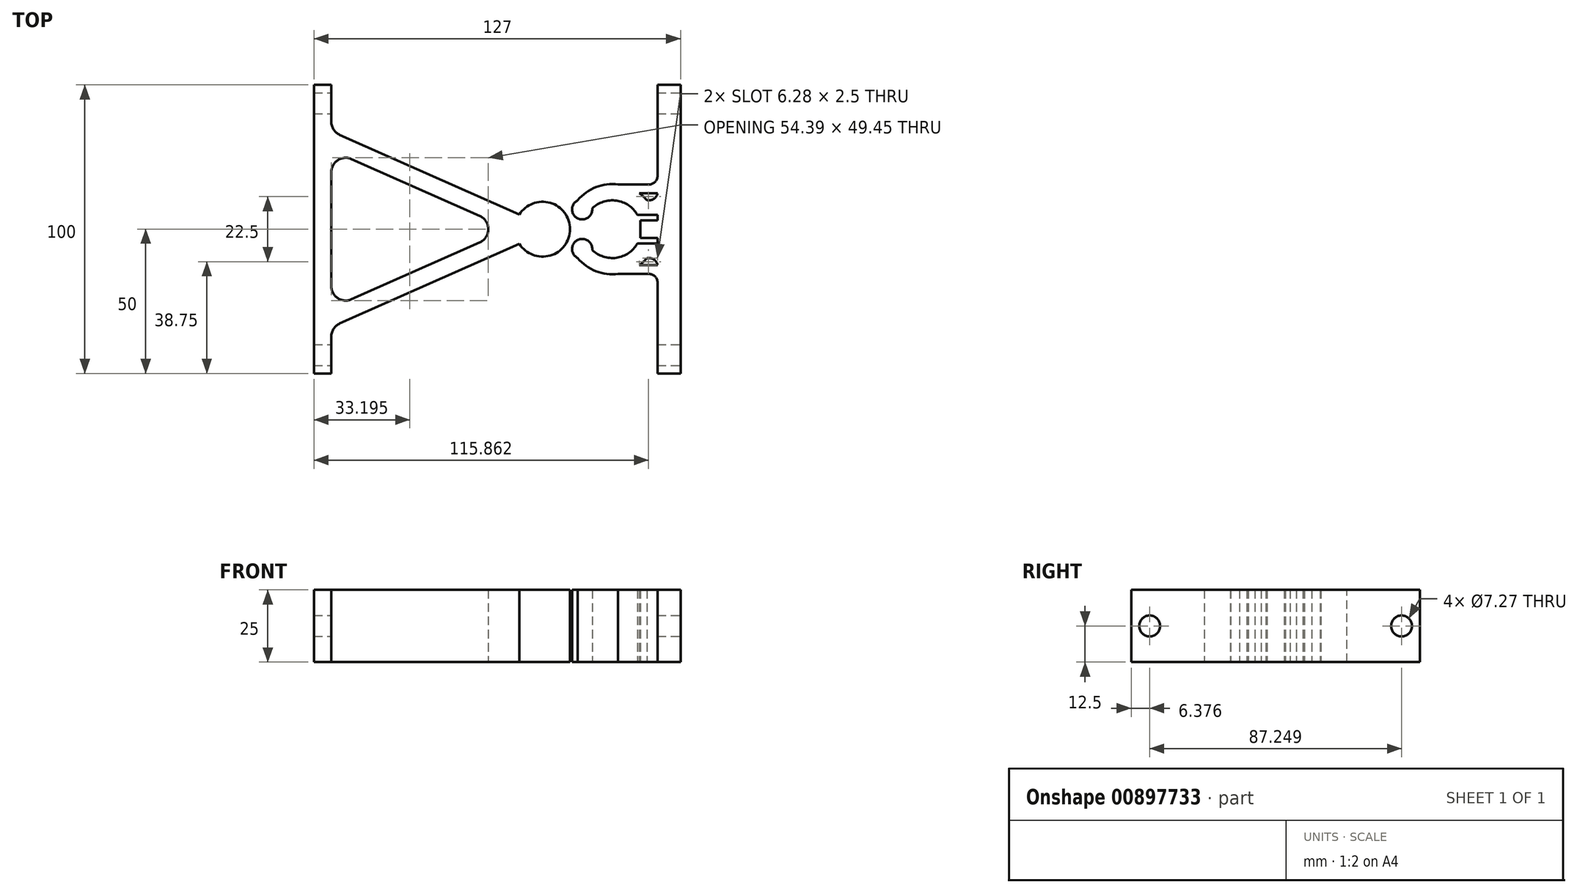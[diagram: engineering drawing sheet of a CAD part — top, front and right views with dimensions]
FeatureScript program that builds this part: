
annotation { "Feature Type Name" : "Feature", "Feature Type Description" : "" }
export const myFeature = defineFeature(function(context is Context, id is Id, definition is map)
    precondition{}
    {
        {
            var Q0;
            Q0=qCreatedBy(makeId("Top.planeOp"),FACE);
            var sketch = newSketch(context, id + "F0", { "sketchPlane" : qUnion([Q0])});
            skLineSegment(sketch, "E0.bottom", {"start": v(3, 50) * mm, "end": v(-3, 50) * mm});
            skLineSegment(sketch, "E0.top", {"start": v(3, -50) * mm, "end": v(-3, -50) * mm});
            skLineSegment(sketch, "E0.left", {"start": v(3, 50) * mm, "end": v(3, -50) * mm});
            skLineSegment(sketch, "E0.right", {"start": v(-3, 50) * mm, "end": v(-3, -50) * mm});
            skPoint(sketch, "E0.middle", {"position": v(0, 0) * mm});
            skCircle(sketch, "E1", {"center": v(76.2, 0) * mm, "radius": 9.5 * mm});
            skLineSegment(sketch, "E2", {"start": v(3, 34) * mm, "end": v(68.14, 5.04) * mm});
            skLineSegment(sketch, "E3", {"start": v(68.14, -5.04) * mm, "end": v(3, -34) * mm});
            skLineSegment(sketch, "E4", {"start": v(64.7, 0) * mm, "end": v(3, -27.43) * mm});
            skLineSegment(sketch, "E5", {"start": v(64.7, 0) * mm, "end": v(3, 27.43) * mm});
            skSolve(sketch);
        }
        {
            var Q0;
            Q0 = qSketchRegion(id + "F0", true);
            extrude(context, id + "F1", {"entities" : qUnion([Q0]), "depth" : 25 * mm, "offsetDistance" : 25 * mm});
        }
        {
            var Q0;
            Q0=makeQuery(id+"F1.opExtrude","SWEPT_EDGE",EDGE,{"disambiguationData":[OSD([sQuery(id+"F0.wireOp",EDGE,"E4"),sQuery(id+"F0.wireOp",EDGE,"E5")])]});
            var Q1;
            Q1=makeQuery(id+"F1.opExtrude","SWEPT_EDGE",EDGE,{"disambiguationData":[OSD([sQuery(id+"F0.wireOp",EDGE,"E0.left"),sQuery(id+"F0.wireOp",EDGE,"E5")])]});
            var Q2;
            Q2=makeQuery(id+"F1.opExtrude","SWEPT_EDGE",EDGE,{"disambiguationData":[OSD([sQuery(id+"F0.wireOp",EDGE,"E0.left"),sQuery(id+"F0.wireOp",EDGE,"E4")])]});
            var Q3;
            Q3=makeQuery(id+"F1.opExtrude","SWEPT_EDGE",EDGE,{"disambiguationData":[OSD([sQuery(id+"F0.wireOp",EDGE,"E0.left"),sQuery(id+"F0.wireOp",EDGE,"E2")])]});
            var Q4;
            Q4=makeQuery(id+"F1.opExtrude","SWEPT_EDGE",EDGE,{"disambiguationData":[OSD([sQuery(id+"F0.wireOp",EDGE,"E0.left"),sQuery(id+"F0.wireOp",EDGE,"E3")])]});
            fillet(context, id + "F2", {"entities" : qUnion([Q0, Q1, Q2, Q3, Q4]), "radius" : 5 * mm, "tangentPropagation" : true, "allowEdgeOverflow" : false});
        }
        {
            var Q0;
            {var subQ0=sQuery(id+"F0.wireOp",EDGE,"E0.left");Q0=makeQuery(id+"F1.opExtrude","SWEPT_FACE",FACE,{"disambiguationData":[OSD([subQ0]),TDD([makeQuery(id+"F0.imprint","IMPRINT",EDGE,{"disambiguationData":[TD([[makeQuery(id+"F0.imprint","INTERSECT",VERTEX,{"derivedFrom":[sQuery(id+"F0.wireOp",EDGE,"E0.top"),subQ0]}),1.0]])],"derivedFrom":subQ0})])]});}
            var sketch = newSketch(context, id + "F3", { "sketchPlane" : qUnion([Q0])});
            skCircle(sketch, "E6", {"center": v(-43.62, 12.5) * mm, "radius": 3.63 * mm});
            skPoint(sketch, "E6.centerSnap0", {"position": v(-43.62, 25) * mm});
            skPoint(sketch, "E6.centerSnap1", {"position": v(-37.25, 12.5) * mm});
            skLineSegment(sketch, "E7", {"start": v(0, -5.63) * mm, "end": v(0, 45.53) * mm, "construction": true});
            skCircle(sketch, "E8.MirrorC", {"center": v(43.62, 12.5) * mm, "radius": 3.63 * mm});
            skSolve(sketch);
        }
        {
            var Q0;
            Q0=qCreatedBy(makeId("Top.planeOp"),FACE);
            var sketch = newSketch(context, id + "F4", { "sketchPlane" : qUnion([Q0])});
            skLineSegment(sketch, "E9.bottom", {"start": v(124, 50) * mm, "end": v(116, 50) * mm});
            skLineSegment(sketch, "E9.top", {"start": v(124, -50) * mm, "end": v(116, -50) * mm});
            skLineSegment(sketch, "E9.left", {"start": v(124, 50) * mm, "end": v(124, -50) * mm});
            skLineSegment(sketch, "E9.right", {"start": v(116, 50) * mm, "end": v(116, -50) * mm});
            skPoint(sketch, "E9.middle", {"position": v(120, 0) * mm});
            skLineSegment(sketch, "E10", {"start": v(1.23, 0) * mm, "end": v(199.45, 0) * mm, "construction": true});
            skLineSegment(sketch, "E11", {"start": v(116, 3) * mm, "end": v(110, 3) * mm});
            skLineSegment(sketch, "E12", {"start": v(110, 3) * mm, "end": v(110, 0) * mm});
            skLineSegment(sketch, "E13", {"start": v(116, 5) * mm, "end": v(115.15, 5) * mm});
            skLineSegment(sketch, "E14", {"start": v(116, 10) * mm, "end": v(112.35, 10) * mm});
            skArc(sketch, "E15", {"start": v(88.33, -10) * mm, "mid": v(100.34, -15.63) * mm, "end": v(112.35, -10) * mm});
            skArc(sketch, "E16.0", {"start": v(93.4, -7.2) * mm, "mid": v(101.73, -9.9) * mm, "end": v(109, -5) * mm});
            skLineSegment(sketch, "E17.MirrorCS", {"start": v(116, -3) * mm, "end": v(110, -3) * mm});
            skLineSegment(sketch, "E18.MirrorCS", {"start": v(110, -3) * mm, "end": v(110, 0) * mm});
            skLineSegment(sketch, "E19.MirrorCS", {"start": v(116, -10) * mm, "end": v(112.35, -10) * mm});
            skLineSegment(sketch, "E20.MirrorCS", {"start": v(116, -5) * mm, "end": v(115.15, -5) * mm});
            skCircle(sketch, "E21", {"center": v(89.91, 6.88) * mm, "radius": 3.5 * mm});
            skCircle(sketch, "E22.MirrorC", {"center": v(89.91, -6.88) * mm, "radius": 3.5 * mm});
            skPoint(sketch, "E23.orphan", {"position": v(85.97, -6.15) * mm});
            skPoint(sketch, "E24.orphan", {"position": v(93.85, -7.61) * mm});
            skPoint(sketch, "E25.orphan", {"position": v(85.97, 6.15) * mm});
            skPoint(sketch, "E26.orphan", {"position": v(93.85, 7.61) * mm});
            skArc(sketch, "E27.trimOffspring", {"start": v(112.35, 10) * mm, "mid": v(100.34, 15.63) * mm, "end": v(88.33, 10) * mm});
            skLineSegment(sketch, "E28", {"start": v(115.15, 5) * mm, "end": v(109, 5) * mm});
            skArc(sketch, "E29.trimOffspring", {"start": v(109, 5) * mm, "mid": v(101.73, 9.9) * mm, "end": v(93.4, 7.2) * mm});
            skLineSegment(sketch, "E30.MirrorCS", {"start": v(115.15, -5) * mm, "end": v(109, -5) * mm});
            skPoint(sketch, "E31.end.orphan", {"position": v(100.34, 10) * mm});
            skPoint(sketch, "E32.MirrorCS.end.orphan", {"position": v(100.34, -10) * mm});
            skPoint(sketch, "E32.MirrorCS.start.orphan", {"position": v(112.35, -10) * mm});
            skLineSegment(sketch, "E33", {"start": v(100.34, -26.06) * mm, "end": v(100.34, 29.63) * mm, "construction": true});
            skPoint(sketch, "E33.startSnap0", {"position": v(100.34, 15.63) * mm});
            skLineSegment(sketch, "E34", {"start": v(102.35, 15.5) * mm, "end": v(116, 15.5) * mm});
            skLineSegment(sketch, "E35", {"start": v(116, 12.5) * mm, "end": v(109.72, 12.5) * mm});
            skLineSegment(sketch, "E36.MirrorCS", {"start": v(116, -12.5) * mm, "end": v(109.72, -12.5) * mm});
            skLineSegment(sketch, "E37.MirrorCS", {"start": v(102.35, -15.5) * mm, "end": v(116, -15.5) * mm});
            skSolve(sketch);
        }
        {
            var Q0;
            Q0 = qSketchRegion(id + "F4", true);
            extrude(context, id + "F5", {"entities" : qUnion([Q0]), "depth" : 25 * mm, "offsetDistance" : 25 * mm});
        }
        {
            var Q0;
            Q0 = qSketchRegion(id + "F3", true);
            extrude(context, id + "F6", {"entities" : qUnion([Q0]), "operationType" : NewBodyOperationType.REMOVE, "endBound" : BoundingType.UP_TO_NEXT, "oppositeDirection" : true, "depth" : 25 * mm, "offsetDistance" : 25 * mm, "hasSecondDirection" : true, "secondDirectionBound" : SecondDirectionBoundingType.THROUGH_ALL, "secondDirectionOppositeDirection" : false, "secondDirectionDepth" : 25 * mm});
        }
        {
            var Q0;
            Q0=makeQuery(id+"F5.opExtrude","SWEPT_EDGE",EDGE,{"disambiguationData":[OSD([sQuery(id+"F4.wireOp",EDGE,"E9.right"),sQuery(id+"F4.wireOp",EDGE,"E14")])]});
            var Q1;
            Q1=makeQuery(id+"F5.opExtrude","SWEPT_EDGE",EDGE,{"disambiguationData":[OSD([sQuery(id+"F4.wireOp",EDGE,"E9.right"),sQuery(id+"F4.wireOp",EDGE,"E19.MirrorCS")])]});
            var Q2;
            Q2=makeQuery(id+"F5.opExtrude","SWEPT_EDGE",EDGE,{"disambiguationData":[OSD([sQuery(id+"F4.wireOp",EDGE,"E9.right"),sQuery(id+"F4.wireOp",EDGE,"E37.MirrorCS")])]});
            var Q3;
            Q3=makeQuery(id+"F5.opExtrude","SWEPT_EDGE",EDGE,{"disambiguationData":[OSD([sQuery(id+"F4.wireOp",EDGE,"E9.right"),sQuery(id+"F4.wireOp",EDGE,"E34")])]});
            fillet(context, id + "F7", {"entities" : qUnion([Q0, Q1, Q2, Q3]), "radius" : 3 * mm, "tangentPropagation" : true, "allowEdgeOverflow" : false});
        }
    });
